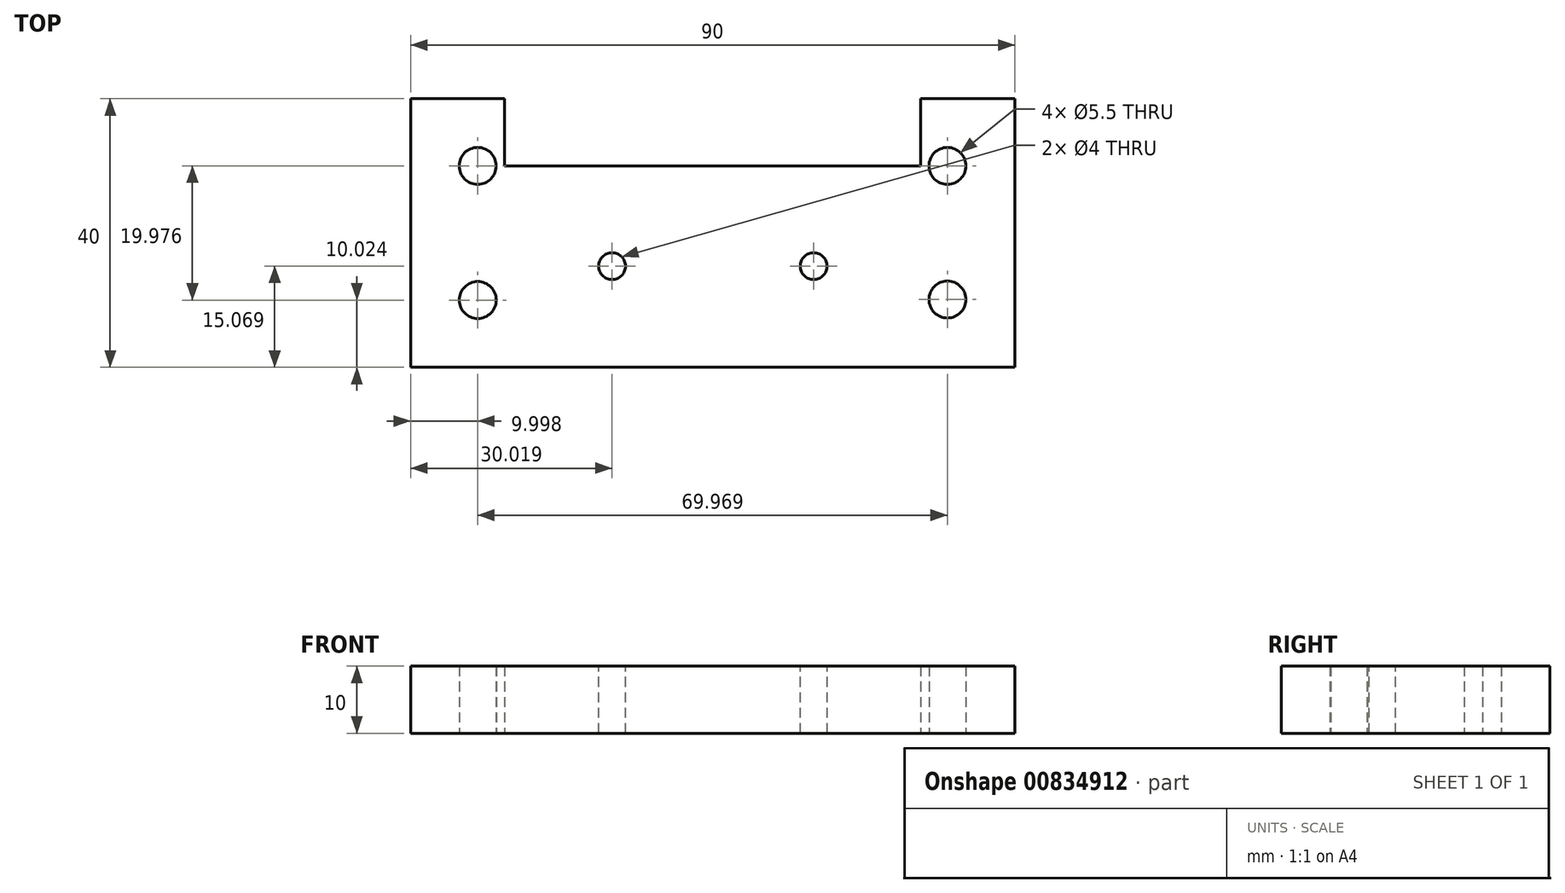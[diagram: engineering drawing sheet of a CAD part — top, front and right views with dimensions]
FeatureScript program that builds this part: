
annotation { "Feature Type Name" : "Feature", "Feature Type Description" : "" }
export const myFeature = defineFeature(function(context is Context, id is Id, definition is map)
    precondition{}
    {
        {
            var Q0;
            Q0=qCreatedBy(makeId("Top.planeOp"),FACE);
            var sketch = newSketch(context, id + "F0", { "sketchPlane" : qUnion([Q0])});
            skLineSegment(sketch, "E0", {"start": v(0, 0) * mm, "end": v(-31, 0) * mm});
            skLineSegment(sketch, "E1", {"start": v(-31, 0) * mm, "end": v(-31, 10) * mm});
            skLineSegment(sketch, "E2", {"start": v(-31, 10) * mm, "end": v(-45, 10) * mm});
            skLineSegment(sketch, "E3", {"start": v(-45, 10) * mm, "end": v(-45, -30) * mm});
            skLineSegment(sketch, "E4", {"start": v(-45, -30) * mm, "end": v(45, -30) * mm});
            skLineSegment(sketch, "E5", {"start": v(45, -30) * mm, "end": v(45, 10) * mm});
            skLineSegment(sketch, "E6", {"start": v(45, 10) * mm, "end": v(31, 10) * mm});
            skLineSegment(sketch, "E7", {"start": v(31, 10) * mm, "end": v(31, 0) * mm});
            skLineSegment(sketch, "E8", {"start": v(31, 0) * mm, "end": v(0, 0) * mm});
            skSolve(sketch);
        }
        {
            var Q0;
            Q0=makeQuery(id+"F0.imprint","IMPRINT",FACE,{"disambiguationData":[TD([[makeQuery(id+"F0.imprint","IMPRINT",EDGE,{"derivedFrom":sQuery(id+"F0.wireOp",EDGE,"E0")}),1.0]])]});
            extrude(context, id + "F1", {"entities" : qUnion([Q0]), "depth" : 5 * mm, "offsetDistance" : 25 * mm});
        }
        {
            var Q0;
            Q0=qCreatedBy(makeId("Top.planeOp"),FACE);
            var sketch = newSketch(context, id + "F2", { "sketchPlane" : qUnion([Q0])});
            skCircle(sketch, "E9", {"center": v(-34.98, -19.98) * mm, "radius": 2.75 * mm});
            skCircle(sketch, "E10", {"center": v(-35, 0) * mm, "radius": 2.75 * mm});
            skCircle(sketch, "E11", {"center": v(34.97, 0) * mm, "radius": 2.75 * mm});
            skCircle(sketch, "E12", {"center": v(34.97, -19.9) * mm, "radius": 2.75 * mm});
            skSolve(sketch);
        }
        {
            var Q0;
            Q0 = qSketchRegion(id + "F2", true);
            extrude(context, id + "F3", {"entities" : qUnion([Q0]), "operationType" : NewBodyOperationType.REMOVE, "depth" : 58.2 * mm, "offsetDistance" : 25 * mm});
        }
        {
            var Q0;
            Q0=makeQuery(id+"F1.opExtrude","CAP_FACE",FACE,{"disambiguationData":[OSD([sQuery(id+"F0.wireOp",EDGE,"E0"),sQuery(id+"F0.wireOp",EDGE,"E1"),sQuery(id+"F0.wireOp",EDGE,"E2"),sQuery(id+"F0.wireOp",EDGE,"E3"),sQuery(id+"F0.wireOp",EDGE,"E4"),sQuery(id+"F0.wireOp",EDGE,"E5"),sQuery(id+"F0.wireOp",EDGE,"E6"),sQuery(id+"F0.wireOp",EDGE,"E7"),sQuery(id+"F0.wireOp",EDGE,"E8")])],"isStart":false});
            var sketch = newSketch(context, id + "F4", { "sketchPlane" : qUnion([Q0])});
            skCircle(sketch, "E13", {"center": v(-14.98, -14.93) * mm, "radius": 2 * mm});
            skCircle(sketch, "E14", {"center": v(15.04, -14.93) * mm, "radius": 2 * mm});
            skSolve(sketch);
        }
        {
            var Q0;
            Q0 = qSketchRegion(id + "F4", true);
            extrude(context, id + "F5", {"entities" : qUnion([Q0]), "operationType" : NewBodyOperationType.REMOVE, "oppositeDirection" : true, "depth" : 25 * mm, "offsetDistance" : 25 * mm});
        }
        {
            var Q0;
            Q0=makeQuery(id+"F1.opExtrude","CAP_FACE",FACE,{"disambiguationData":[OSD([sQuery(id+"F0.wireOp",EDGE,"E0"),sQuery(id+"F0.wireOp",EDGE,"E1"),sQuery(id+"F0.wireOp",EDGE,"E2"),sQuery(id+"F0.wireOp",EDGE,"E3"),sQuery(id+"F0.wireOp",EDGE,"E4"),sQuery(id+"F0.wireOp",EDGE,"E5"),sQuery(id+"F0.wireOp",EDGE,"E6"),sQuery(id+"F0.wireOp",EDGE,"E7"),sQuery(id+"F0.wireOp",EDGE,"E8")])],"isStart":false});
            extrude(context, id + "F6", {"entities" : qUnion([Q0]), "operationType" : NewBodyOperationType.ADD, "depth" : 5 * mm, "offsetDistance" : 25 * mm});
        }
    });
